# Revit family: Hohldeckenanker Easy
name_source: partatom
category: HLS-Bauteile
units: mm (PartAtom-declared; Revit-internal decimal feet)

## family parameters
Basisbauteil = Fläche
Beim Laden mit Abzugskörper schneiden = Nein
Bemaßung runder Anschluss = Durchmesser verwenden
Beschriftungsausrichtung beibehalten = Nein
Gemeinsam genutzt = Ja
Raumberechnungspunkt = Nein
Teiletyp = Normal

## types (2) — shared parameters
Bohrerdurchmesser = 12 mm
Fabrikat = MKT
Firma = MEFA Befestigungs- und Montagesysteme GmbH
Gewicht pro Bauteil = 0.02 kg
Kurztext1 = Hohldeckenanker Easy
Material = Stahl
Mengeneinheit = St
Vorgabe-Ansicht = 1219 mm
vpe = 50
zero-valued in all types: Länge Gewinde

## per-type parameters (varying)
| type | Artikelnummer | Bohrlochtiefe | D | EAN | Gewicht | Gewinde | Hülsenlänge | Kurztext2 | Länge | Setztiefe | T | d1 |
| Easy M8 | 221851100101 | 55 mm | 5 mm  [stored 0.0164042 ft] | 4043315047861 | 0.01 kg | M8 | 35 mm | M8 | 35 mm  [stored 0.114829 ft] | 47 mm | 55 mm  [stored 0.180446 ft] | 7 mm  [stored 0.0229659 ft] |
| Easy M10 | 221851200101 | 60 mm | 7 mm  [stored 0.0229659 ft] | 4043315047878 | 0.03 kg | M10 | 40 mm | M10 | 40 mm  [stored 0.131234 ft] | 55 mm | 60 mm  [stored 0.19685 ft] | 9 mm  [stored 0.0295276 ft] |

note: [stored X ft] marks values corroborated as IEEE doubles in the binary element streams (Revit-internal decimal feet)
